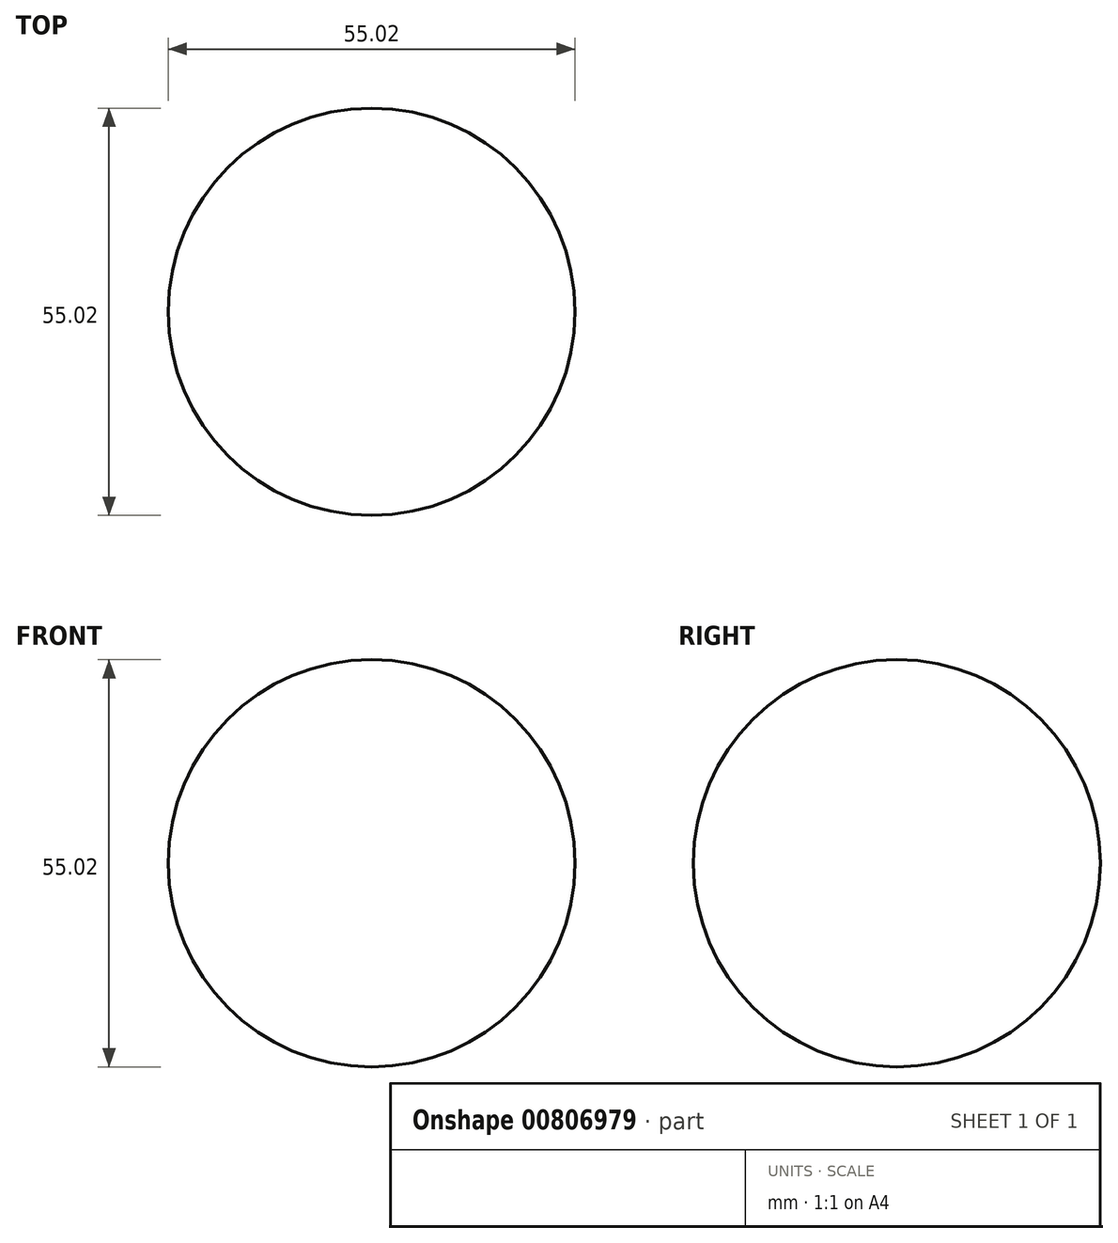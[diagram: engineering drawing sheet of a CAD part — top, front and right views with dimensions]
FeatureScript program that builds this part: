
annotation { "Feature Type Name" : "Feature", "Feature Type Description" : "" }
export const myFeature = defineFeature(function(context is Context, id is Id, definition is map)
    precondition{}
    {
        {
            var Q0;
            Q0=qCreatedBy(makeId("Front.planeOp"),FACE);
            var sketch = newSketch(context, id + "F0", { "sketchPlane" : qUnion([Q0])});
            skCircle(sketch, "E0", {"center": v(0, 0) * mm, "radius": 27.51 * mm});
            skLineSegment(sketch, "E1", {"start": v(0, -51.34) * mm, "end": v(0, 54.84) * mm});
            skSolve(sketch);
        }
        {
            var Q0;
            {var subQ0=sQuery(id+"F0.wireOp",EDGE,"E1");var subQ1=sQuery(id+"F0.wireOp",EDGE,"E0");var subQ2=makeQuery(id+"F0.imprint","INTERSECT",VERTEX,{"disambiguationData":[OD(0.0)],"derivedFrom":[subQ1,subQ0]});Q0=makeQuery(id+"F0.imprint","IMPRINT",FACE,{"disambiguationData":[TD([[makeQuery(id+"F0.imprint","IMPRINT",EDGE,{"disambiguationData":[TD([[subQ2,-1.0]])],"derivedFrom":subQ1}),1.0]])]});}
            var Q1;
            Q1=sQuery(id+"F0.wireOp",EDGE,"E1");
            revolve(context, id + "F1", {"surfaceOperationType" : NewSurfaceOperationType.NEW, "entities" : qUnion([Q0]), "axis" : qUnion([Q1]), "revolveType" : RevolveType.FULL});
        }
    });
